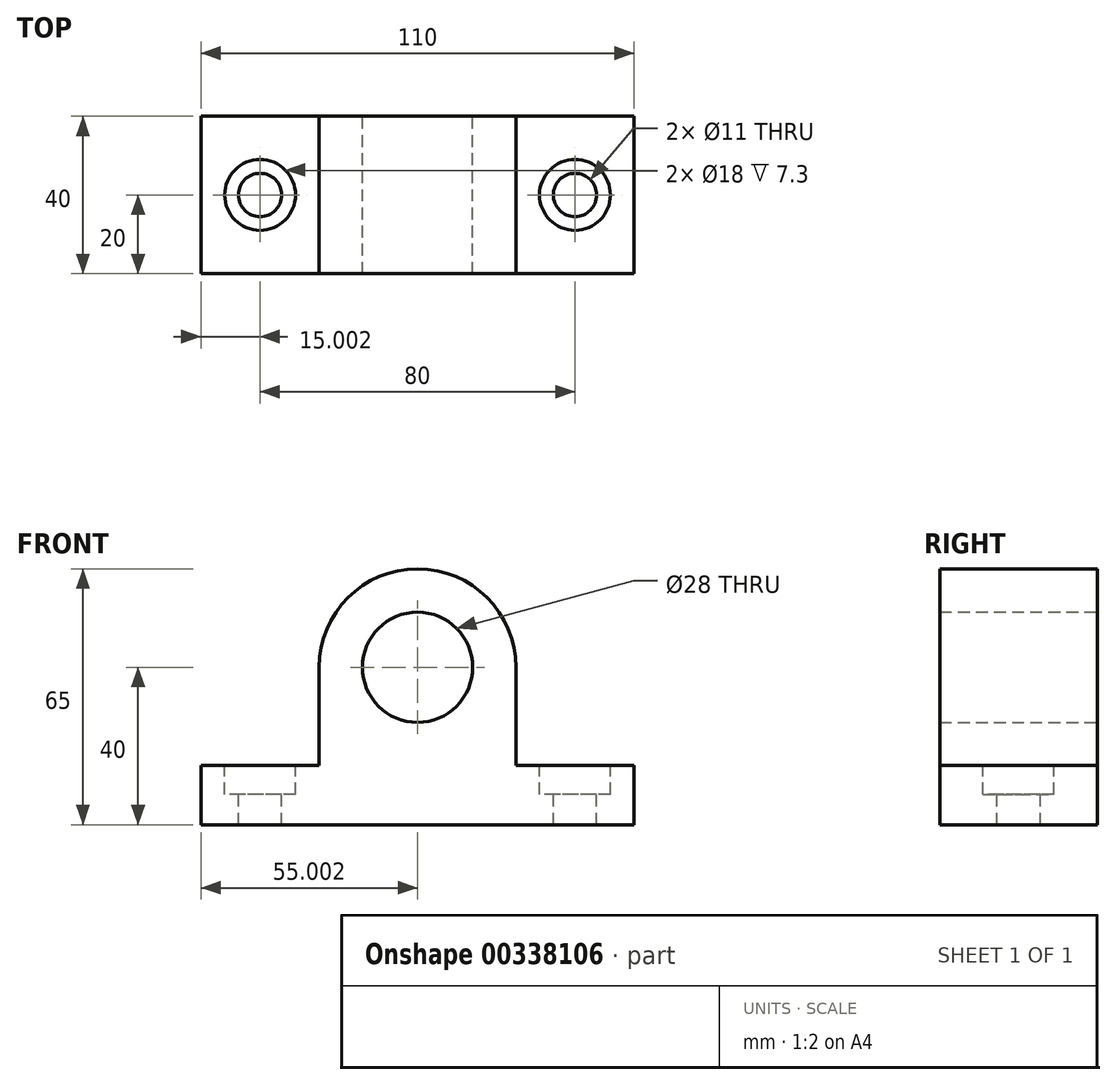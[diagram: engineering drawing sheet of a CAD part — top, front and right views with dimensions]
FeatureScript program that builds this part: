
annotation { "Feature Type Name" : "Feature", "Feature Type Description" : "" }
export const myFeature = defineFeature(function(context is Context, id is Id, definition is map)
    precondition{}
    {
        {
            var Q0;
            Q0=qCreatedBy(makeId("Front.planeOp"),FACE);
            var sketch = newSketch(context, id + "F0", { "sketchPlane" : qUnion([Q0])});
            skLineSegment(sketch, "E0", {"start": v(-31.93, 7.7) * mm, "end": v(-31.93, 0) * mm});
            skLineSegment(sketch, "E1", {"start": v(-31.93, 0) * mm, "end": v(78.07, 0) * mm});
            skLineSegment(sketch, "E2", {"start": v(78.07, 0) * mm, "end": v(78.07, 7.7) * mm});
            skCircle(sketch, "E3", {"center": v(23.07, 40) * mm, "radius": 14 * mm});
            skLineSegment(sketch, "E4", {"start": v(-31.93, 7.7) * mm, "end": v(-31.93, 15) * mm});
            skLineSegment(sketch, "E5", {"start": v(-31.93, 15) * mm, "end": v(-1.93, 15) * mm});
            skLineSegment(sketch, "E6", {"start": v(78.07, 7.7) * mm, "end": v(78.07, 15) * mm});
            skLineSegment(sketch, "E7", {"start": v(78.07, 15) * mm, "end": v(48.07, 15) * mm});
            skLineSegment(sketch, "E8", {"start": v(-1.93, 27.34) * mm, "end": v(-1.93, 15) * mm});
            skLineSegment(sketch, "E9", {"start": v(48.07, 27.34) * mm, "end": v(48.07, 15) * mm});
            skLineSegment(sketch, "E10", {"start": v(-1.93, 27.34) * mm, "end": v(-1.93, 40) * mm});
            skLineSegment(sketch, "E11", {"start": v(48.07, 27.34) * mm, "end": v(48.07, 40) * mm});
            skArc(sketch, "E12", {"start": v(48.07, 40) * mm, "mid": v(23.07, 65) * mm, "end": v(-1.93, 40) * mm});
            skSolve(sketch);
        }
        {
            var Q0;
            Q0 = qSketchRegion(id + "F0", true);
            extrude(context, id + "F1", {"entities" : qUnion([Q0]), "depth" : 40 * mm});
        }
        {
            var Q0;
            Q0=makeQuery(id+"F1.opExtrude","SWEPT_FACE",FACE,{"disambiguationData":[OSD([sQuery(id+"F0.wireOp",EDGE,"E7")])]});
            var sketch = newSketch(context, id + "F2", { "sketchPlane" : qUnion([Q0])});
            skCircle(sketch, "E13", {"center": v(63.07, -20) * mm, "radius": 9 * mm});
            skSolve(sketch);
        }
        {
            var Q0;
            Q0=makeQuery(id+"F1.opExtrude","SWEPT_FACE",FACE,{"disambiguationData":[OSD([sQuery(id+"F0.wireOp",EDGE,"E5")])]});
            var sketch = newSketch(context, id + "F3", { "sketchPlane" : qUnion([Q0])});
            skCircle(sketch, "E14", {"center": v(-16.93, -20) * mm, "radius": 9 * mm});
            skSolve(sketch);
        }
        {
            var Q0;
            Q0=sQuery(id+"F3.wireOp",VERTEX,"E14.center");
            var Q1;
            Q1=sQuery(id+"F2.wireOp",VERTEX,"E13.center");
            var Q2;
            Q2=makeQuery(id+"F1.opExtrude","SWEPT_BODY",BODY,{"disambiguationData":[OSD([sQuery(id+"F0.wireOp",EDGE,"E0"),sQuery(id+"F0.wireOp",EDGE,"E1"),sQuery(id+"F0.wireOp",EDGE,"E2"),sQuery(id+"F0.wireOp",EDGE,"E3"),sQuery(id+"F0.wireOp",EDGE,"E4"),sQuery(id+"F0.wireOp",EDGE,"E5"),sQuery(id+"F0.wireOp",EDGE,"E6"),sQuery(id+"F0.wireOp",EDGE,"E7"),sQuery(id+"F0.wireOp",EDGE,"E8"),sQuery(id+"F0.wireOp",EDGE,"E9"),sQuery(id+"F0.wireOp",EDGE,"E10"),sQuery(id+"F0.wireOp",EDGE,"E11"),sQuery(id+"F0.wireOp",EDGE,"E12")])]});
            hole(context, id + "F4", {"style" : HoleStyle.C_BORE, "endStyle" : HoleEndStyle.THROUGH, "holeDiameter" : 11 * mm, "cBoreDiameter" : 18 * mm, "cBoreDepth" : 7.3 * mm, "tappedDepth" : 12 * mm, "tapClearance" : 3, "locations" : qUnion([Q0, Q1]), "scope" : qUnion([Q2])});
        }
    });
